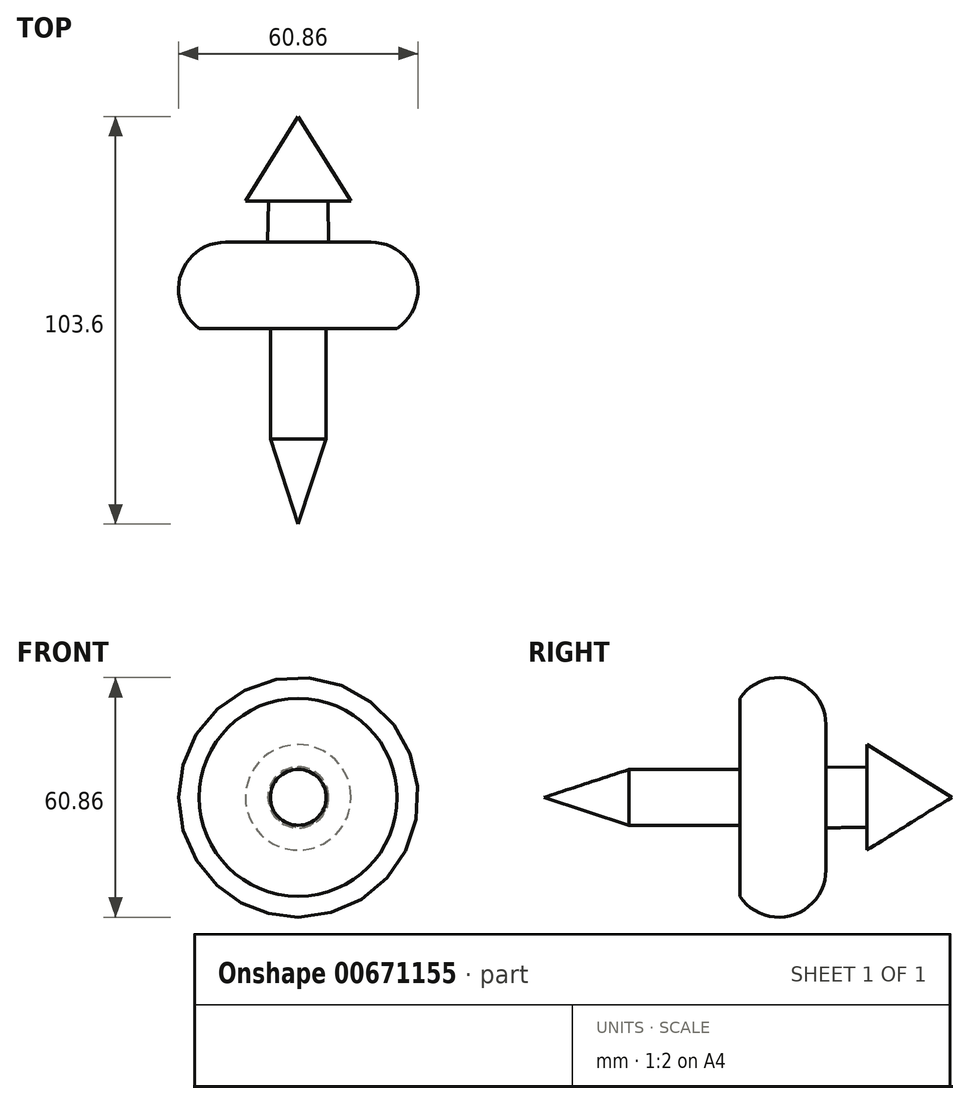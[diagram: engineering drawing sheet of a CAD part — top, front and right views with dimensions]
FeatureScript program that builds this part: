
annotation { "Feature Type Name" : "Feature", "Feature Type Description" : "" }
export const myFeature = defineFeature(function(context is Context, id is Id, definition is map)
    precondition{}
    {
        {
            var Q0;
            Q0=qCreatedBy(makeId("Right.planeOp"),FACE);
            var sketch = newSketch(context, id + "F0", { "sketchPlane" : qUnion([Q0])});
            skLineSegment(sketch, "E0", {"start": v(-26.81, 0) * mm, "end": v(-26.81, 25.15) * mm});
            skLineSegment(sketch, "E1", {"start": v(-26.81, 0) * mm, "end": v(0, 0) * mm});
            skLineSegment(sketch, "E2", {"start": v(0, 0) * mm, "end": v(27.04, 0) * mm});
            skLineSegment(sketch, "E3", {"start": v(27.04, 0) * mm, "end": v(5.5, 13.4) * mm});
            skLineSegment(sketch, "E4", {"start": v(5.5, 13.4) * mm, "end": v(5.5, 7.58) * mm});
            skLineSegment(sketch, "E5", {"start": v(5.5, 7.58) * mm, "end": v(-4.93, 7.75) * mm});
            skLineSegment(sketch, "E6", {"start": v(-4.93, 7.75) * mm, "end": v(-4.93, 18.47) * mm});
            skArc(sketch, "E7", {"start": v(-4.93, 18.47) * mm, "mid": v(-13.4, 29.91) * mm, "end": v(-26.81, 25.15) * mm});
            skSolve(sketch);
        }
        {
            var Q0;
            Q0=qSketchRegion(id+"F0",true);
            var Q1;
            Q1=sQuery(id+"F0.wireOp",EDGE,"E1");
            revolve(context, id + "F1", {"entities" : qUnion([Q0]), "axis" : qUnion([Q1]), "revolveType" : RevolveType.FULL});
        }
        {
            var Q0;
            Q0=qCreatedBy(makeId("Right.planeOp"),FACE);
            var sketch = newSketch(context, id + "F2", { "sketchPlane" : qUnion([Q0])});
            skLineSegment(sketch, "E8.bottom", {"start": v(-54.94, 7.09) * mm, "end": v(0, 7.09) * mm});
            skLineSegment(sketch, "E8.top", {"start": v(-54.94, 0) * mm, "end": v(0, 0) * mm});
            skLineSegment(sketch, "E8.left", {"start": v(-54.94, 7.09) * mm, "end": v(-54.94, 0) * mm});
            skLineSegment(sketch, "E8.right", {"start": v(0, 7.09) * mm, "end": v(0, 0) * mm});
            skLineSegment(sketch, "E9", {"start": v(-76.56, 0) * mm, "end": v(-54.94, 7.09) * mm});
            skLineSegment(sketch, "E10", {"start": v(-76.56, 0) * mm, "end": v(-54.94, 0) * mm});
            skSolve(sketch);
        }
        {
            var Q0;
            Q0=qSketchRegion(id+"F2",true);
            var Q1;
            Q1=sQuery(id+"F2.wireOp",EDGE,"E8.top");
            revolve(context, id + "F3", {"operationType" : NewBodyOperationType.ADD, "entities" : qUnion([Q0]), "axis" : qUnion([Q1]), "revolveType" : RevolveType.FULL});
        }
    });
